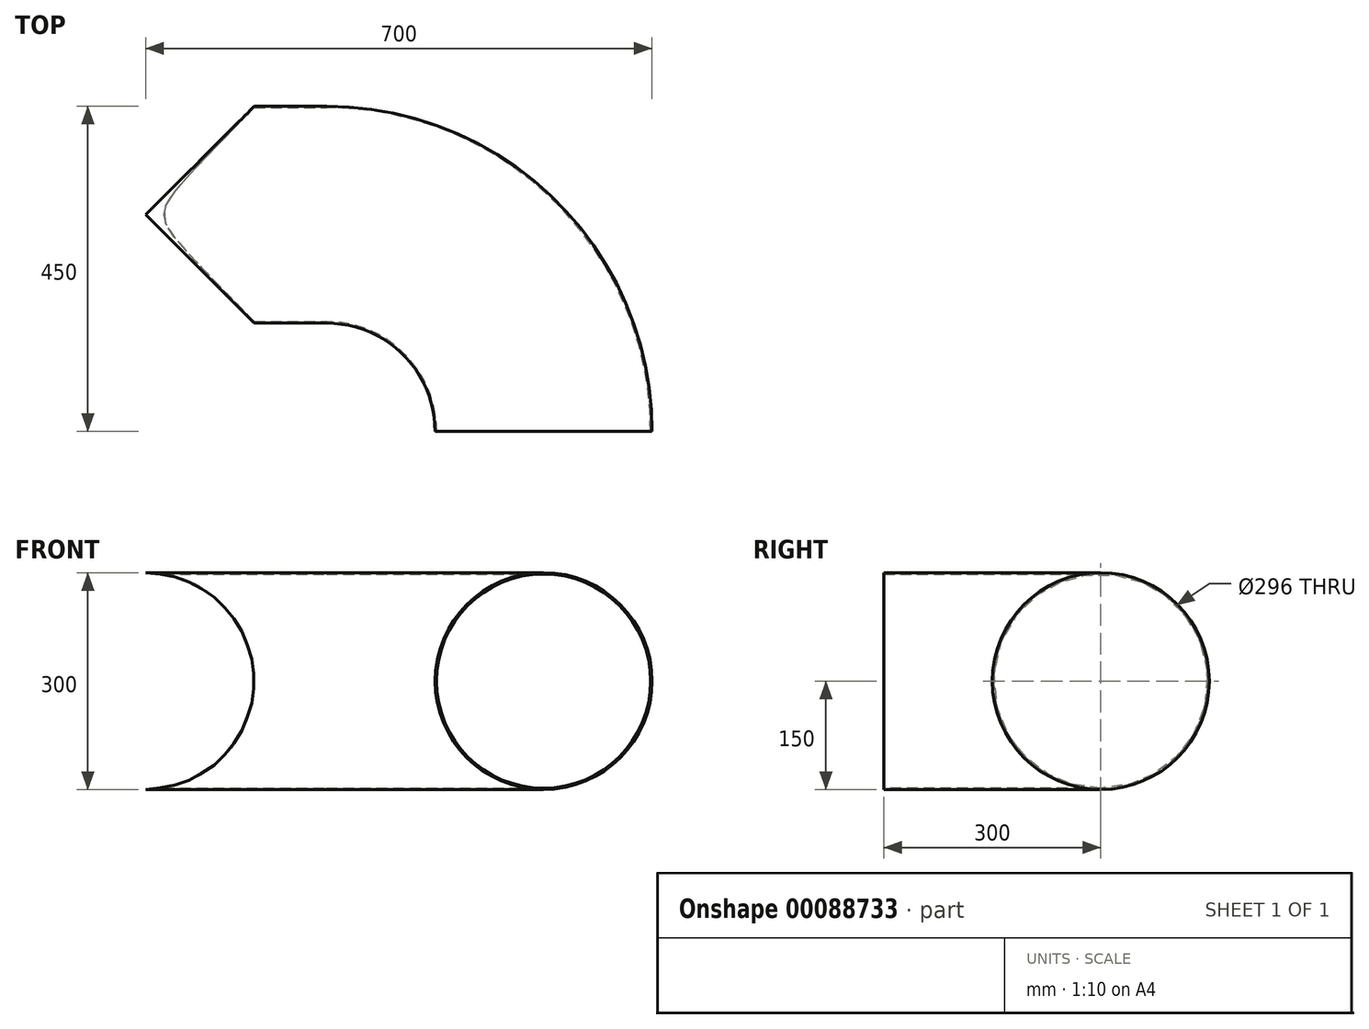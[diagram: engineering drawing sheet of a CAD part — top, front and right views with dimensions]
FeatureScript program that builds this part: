
annotation { "Feature Type Name" : "Feature", "Feature Type Description" : "" }
export const myFeature = defineFeature(function(context is Context, id is Id, definition is map)
    precondition{}
    {
        {
            var Q0;
            Q0=qCreatedBy(makeId("Right.planeOp"),FACE);
            var sketch = newSketch(context, id + "F0", { "sketchPlane" : qUnion([Q0])});
            skCircle(sketch, "E0", {"center": v(0, 0) * mm, "radius": 150 * mm});
            skCircle(sketch, "E1", {"center": v(0, 0) * mm, "radius": 148 * mm});
            skSolve(sketch);
        }
        {
            var Q0;
            Q0=qCreatedBy(makeId("Top.planeOp"),FACE);
            var sketch = newSketch(context, id + "F1", { "sketchPlane" : qUnion([Q0])});
            skLineSegment(sketch, "E2", {"start": v(0, 0) * mm, "end": v(250, 0) * mm});
            skLineSegment(sketch, "E3", {"start": v(550, -300) * mm, "end": v(550, -300) * mm});
            skPoint(sketch, "E4.visualSharp", {"position": v(550, 0) * mm});
            skArc(sketch, "E4.filletArc", {"start": v(550, -300) * mm, "mid": v(462.13, -87.87) * mm, "end": v(250, 0) * mm});
            skSolve(sketch);
        }
        {
            var Q0;
            Q0=makeQuery(id+"F0.imprint","IMPRINT",FACE,{"disambiguationData":[TD([[makeQuery(id+"F0.imprint","IMPRINT",EDGE,{"derivedFrom":sQuery(id+"F0.wireOp",EDGE,"E0")}),1.0]])]});
            var Q1;
            Q1=sQuery(id+"F1.wireOp",EDGE,"E2");
            var Q2;
            Q2=sQuery(id+"F1.wireOp",EDGE,"E4.filletArc");
            var Q3;
            Q3=sQuery(id+"F1.wireOp",EDGE,"E3");
            sweep(context, id + "F2", {"profiles" : qUnion([Q0]), "path" : qUnion([Q1, Q2, Q3])});
        }
        {
            var Q0;
            Q0=qCreatedBy(makeId("Front.planeOp"),FACE);
            var sketch = newSketch(context, id + "F3", { "sketchPlane" : qUnion([Q0])});
            skCircle(sketch, "E5", {"center": v(0, 0) * mm, "radius": 150 * mm});
            skSolve(sketch);
        }
        {
            var Q0;
            Q0=makeQuery(id+"F3.imprint","IMPRINT",FACE,{"disambiguationData":[TD([[makeQuery(id+"F3.imprint","IMPRINT",EDGE,{"derivedFrom":sQuery(id+"F3.wireOp",EDGE,"E5")}),1.0]])]});
            extrude(context, id + "F4", {"entities" : qUnion([Q0]), "operationType" : NewBodyOperationType.REMOVE, "endBound" : BoundingType.THROUGH_ALL, "depth" : 25 * mm, "hasSecondDirection" : true, "secondDirectionBound" : BoundingType.THROUGH_ALL, "secondDirectionOppositeDirection" : true, "secondDirectionDepth" : 25 * mm});
        }
    });
